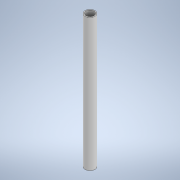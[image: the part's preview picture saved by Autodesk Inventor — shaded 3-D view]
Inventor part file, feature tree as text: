
AUTODESK INVENTOR PART (.ipt)
format: ipt  version: 2020 (Build 240168000, 168)  size: 93,184 bytes
history: native  units: mm
features: extrude x1, sketch x1
ambient origin geometry x8: Origin, YZ Plane, XZ Plane, XY Plane, X Axis, Y Axis, Z Axis, Center Point
bodies: Solid1 (feature_tree)
feature tree (2):
  extrude  "Extrusion1"  Depth=200.0mm
  sketch  "Sketch1"  dims[d0=15.0mm d1=12.0mm d2=200.0mm d3=0.0mm]
